# Revit family: Wye_Pattern_Strainers-Backflow_Preventor-WATTS-88CSI
name_source: partatom
category: Pipe Accessories
revit_build: Autodesk Revit 2014 (Build: 20130308_1515(x64)
units: mm (PartAtom-declared; Revit-internal decimal feet)

## types (6) — shared parameters
Assembly Code = F1050
CW Connection = Yes
Country = United States
Description = Cast Iron, Wye-Pattern Strainers
Finish = Metal-WATTS-Class 600-Cast Steel
HW Connection = No
Manufacturer = WATTS
Manufacturer Product Line = Strainers
Material = Metal-WATTS-Class 600-Cast Steel
Max. Working Pressure = 600psi (41.4 bar) at 489°F (254°C) WSP 1480psi (102.0 bar) at 100°F (38°C) WOG
Model = 77SI
Price = Prices may vary. Please consult Manufacturer Representative for most up-to-date price list.
Product Documentation Link = http://media.wattswater.com
Product Page URL = http://www.watts.com
Region = North America
URL = http://www.watts.com
Vent Connection = No
Warranty Information = 1 Year Limited Warranty
Waste Connection = No

## per-type parameters (varying)
| type | A | B | Connection Inlet Description | Connection Outlet Description | Connection Radius | Connection Size | NPT Diameter | NPT Radius | Nominal Depth | Nominal Height | Nominal Length | Nominal Length 2 | Nominal Radius 2 | Nominal Width | Weight | Width |
| 88CSI  - 0.5" | 2 15/16" | 2 1/4" | 1/2" NPT Flanged Inlet | 1/2" NPT Flanged Outlet | 1/4" | 1/2" | 1/4" | 1/8" | 5/16" | 19/32" | 5/8" | 1 1/8" | 19/32" | 29/32" | 2/0.9 (LB/KG) | 1 1/8" |
| 88CSI  - 0.75" | 3 7/16" | 2 9/16" | 3/4" NPT Flanged Inlet | 3/4" NPT Flanged Outlet | 3/8" | 3/4" | 3/8" | 3/16" | 5/16" | 21/32" | 23/32" | 1 9/32" | 21/32" | 1" | 3/1.3 (LB/KG) | 1 1/8" |
| 88CSI  - 1" | 4 9/16" | 2 13/16" | 1" NPT Flanged Inlet | 1" NPT Flanged Outlet | 1/2" | 1" | 3/8" | 3/16" | 3/8" | 3/4" | 13/16" | 1 7/16" | 3/4" | 1 1/8" | 5/2.2 (LB/KG) | 1 3/8" |
| 88CSI  - 1.25" | 4 15/16" | 3 1/16" | 1-1/4" NPT Flanged Inlet | 1-1/4" NPT Flanged Outlet | 5/8" | 1 1/4" | 3/4" | 3/8" | 3/8" | 1" | 1 1/8" | 1 7/8" | 1" | 1 1/2" | 7/3.1 (LB/KG) | 1 5/8" |
| 88CSI  - 1.5" | 5 9/16" | 3 5/16" | 1-1/2" NPT Flanged Inlet | 1-1/2" NPT Flanged Outlet | 3/4" | 1 1/2" | 3/4" | 3/8" | 1/2" | 1 1/8" | 1 5/16" | 2 3/16" | 1 1/8" | 1 3/4" | 10/4.5 (LB/KG) | 2" |
| 88CSI  - 2" | 6 15/16" | 4 13/16" | 2" NPT Flanged Inlet | 2" NPT Flanged Outlet | 1" | 2" | 1" | 1/2" | 1/2" | 1 3/8" | 1 3/4" | 2 25/32" | 1 3/8" | 2 1/8" | 15/6.8 (LB/KG) | 2 3/4" |

## geometry (parser evidence)
native form markers: Sweep x1
no freeform markers — native parametric forms only
